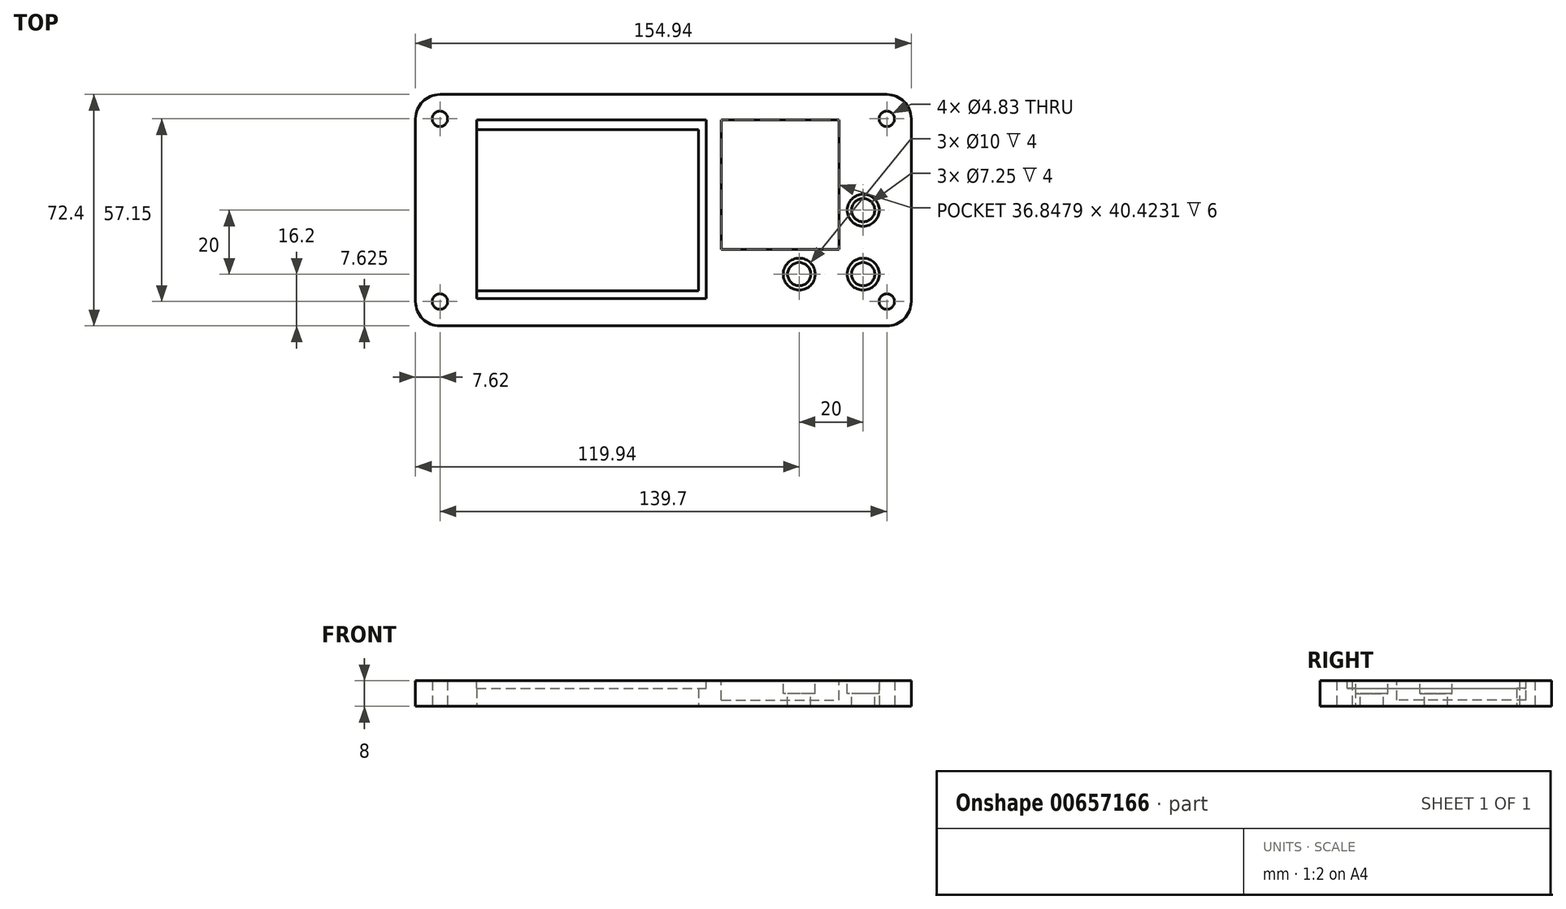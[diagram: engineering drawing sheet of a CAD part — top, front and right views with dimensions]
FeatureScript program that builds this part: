
annotation { "Feature Type Name" : "Feature", "Feature Type Description" : "" }
export const myFeature = defineFeature(function(context is Context, id is Id, definition is map)
    precondition{}
    {
        {
            var Q0;
            Q0=qCreatedBy(makeId("Top.planeOp"),FACE);
            var sketch = newSketch(context, id + "F0", { "sketchPlane" : qUnion([Q0])});
            skCircle(sketch, "E0", {"center": v(-69.85, 28.58) * mm, "radius": 2.41 * mm});
            skCircle(sketch, "E1.MirrorC", {"center": v(69.85, 28.58) * mm, "radius": 2.41 * mm});
            skCircle(sketch, "E2.MirrorC", {"center": v(-69.85, -28.58) * mm, "radius": 2.41 * mm});
            skCircle(sketch, "E3.MirrorC", {"center": v(69.85, -28.58) * mm, "radius": 2.41 * mm});
            skLineSegment(sketch, "E4", {"start": v(-77.47, 28.58) * mm, "end": v(-77.47, 0) * mm});
            skLineSegment(sketch, "E5", {"start": v(-69.85, 36.2) * mm, "end": v(0, 36.2) * mm});
            skLineSegment(sketch, "E6.MirrorCS", {"start": v(77.47, 28.58) * mm, "end": v(77.47, 0) * mm});
            skLineSegment(sketch, "E7.MirrorCS", {"start": v(69.85, 36.2) * mm, "end": v(0, 36.2) * mm});
            skLineSegment(sketch, "E8.MirrorCS", {"start": v(-77.47, -28.58) * mm, "end": v(-77.47, 0) * mm});
            skLineSegment(sketch, "E9.MirrorCS", {"start": v(-69.85, -36.2) * mm, "end": v(0, -36.2) * mm});
            skLineSegment(sketch, "E10.MirrorCS", {"start": v(69.85, -36.2) * mm, "end": v(0, -36.2) * mm});
            skLineSegment(sketch, "E11.MirrorCS", {"start": v(77.47, -28.58) * mm, "end": v(77.47, 0) * mm});
            skArc(sketch, "E12", {"start": v(-69.85, 36.2) * mm, "mid": v(-75.24, 33.96) * mm, "end": v(-77.47, 28.58) * mm});
            skArc(sketch, "E13.MirrorCS", {"start": v(69.85, 36.2) * mm, "mid": v(75.24, 33.96) * mm, "end": v(77.47, 28.58) * mm});
            skArc(sketch, "E14.MirrorCS", {"start": v(-69.85, -36.2) * mm, "mid": v(-75.24, -33.96) * mm, "end": v(-77.47, -28.58) * mm});
            skArc(sketch, "E15.MirrorCS", {"start": v(69.85, -36.2) * mm, "mid": v(75.24, -33.96) * mm, "end": v(77.47, -28.58) * mm});
            skSolve(sketch);
        }
        {
            var Q0;
            Q0=makeQuery(id+"F0.imprint","IMPRINT",FACE,{"disambiguationData":[TD([[makeQuery(id+"F0.imprint","IMPRINT",EDGE,{"derivedFrom":sQuery(id+"F0.wireOp",EDGE,"E0")}),-1.0]])]});
            extrude(context, id + "F1", {"entities" : qUnion([Q0]), "depth" : 8 * mm, "offsetDistance" : 25.4 * mm});
        }
        {
            var Q0;
            Q0=makeQuery(id+"F1.opExtrude","CAP_FACE",FACE,{"disambiguationData":[OSD([sQuery(id+"F0.wireOp",EDGE,"E0"),sQuery(id+"F0.wireOp",EDGE,"E1.MirrorC"),sQuery(id+"F0.wireOp",EDGE,"E2.MirrorC"),sQuery(id+"F0.wireOp",EDGE,"E3.MirrorC"),sQuery(id+"F0.wireOp",EDGE,"E4"),sQuery(id+"F0.wireOp",EDGE,"E5"),sQuery(id+"F0.wireOp",EDGE,"E6.MirrorCS"),sQuery(id+"F0.wireOp",EDGE,"E7.MirrorCS"),sQuery(id+"F0.wireOp",EDGE,"E8.MirrorCS"),sQuery(id+"F0.wireOp",EDGE,"E9.MirrorCS"),sQuery(id+"F0.wireOp",EDGE,"E10.MirrorCS"),sQuery(id+"F0.wireOp",EDGE,"E11.MirrorCS"),sQuery(id+"F0.wireOp",EDGE,"E12"),sQuery(id+"F0.wireOp",EDGE,"E13.MirrorCS"),sQuery(id+"F0.wireOp",EDGE,"E14.MirrorCS"),sQuery(id+"F0.wireOp",EDGE,"E15.MirrorCS")])],"isStart":true});
            var sketch = newSketch(context, id + "F2", { "sketchPlane" : qUnion([Q0])});
            skLineSegment(sketch, "E16.bottom", {"start": v(-58.42, 25.2) * mm, "end": v(10.94, 25.2) * mm});
            skLineSegment(sketch, "E16.top", {"start": v(-58.42, -25.2) * mm, "end": v(10.94, -25.2) * mm});
            skLineSegment(sketch, "E16.left", {"start": v(-58.42, 25.2) * mm, "end": v(-58.42, -25.2) * mm});
            skLineSegment(sketch, "E16.right", {"start": v(10.94, 25.2) * mm, "end": v(10.94, -25.2) * mm});
            skSolve(sketch);
        }
        {
            var Q0;
            Q0=makeQuery(id+"F2.imprint","IMPRINT",FACE,{"disambiguationData":[TD([[makeQuery(id+"F2.imprint","IMPRINT",EDGE,{"derivedFrom":sQuery(id+"F2.wireOp",EDGE,"E16.bottom")}),-1.0]])]});
            extrude(context, id + "F3", {"entities" : qUnion([Q0]), "operationType" : NewBodyOperationType.REMOVE, "oppositeDirection" : true, "depth" : 25.4 * mm, "offsetDistance" : 25.4 * mm});
        }
        {
            var Q0;
            Q0=makeQuery(id+"F1.opExtrude","CAP_FACE",FACE,{"disambiguationData":[OSD([sQuery(id+"F0.wireOp",EDGE,"E0"),sQuery(id+"F0.wireOp",EDGE,"E1.MirrorC"),sQuery(id+"F0.wireOp",EDGE,"E2.MirrorC"),sQuery(id+"F0.wireOp",EDGE,"E3.MirrorC"),sQuery(id+"F0.wireOp",EDGE,"E4"),sQuery(id+"F0.wireOp",EDGE,"E5"),sQuery(id+"F0.wireOp",EDGE,"E6.MirrorCS"),sQuery(id+"F0.wireOp",EDGE,"E7.MirrorCS"),sQuery(id+"F0.wireOp",EDGE,"E8.MirrorCS"),sQuery(id+"F0.wireOp",EDGE,"E9.MirrorCS"),sQuery(id+"F0.wireOp",EDGE,"E10.MirrorCS"),sQuery(id+"F0.wireOp",EDGE,"E11.MirrorCS"),sQuery(id+"F0.wireOp",EDGE,"E12"),sQuery(id+"F0.wireOp",EDGE,"E13.MirrorCS"),sQuery(id+"F0.wireOp",EDGE,"E14.MirrorCS"),sQuery(id+"F0.wireOp",EDGE,"E15.MirrorCS")])],"isStart":false});
            var sketch = newSketch(context, id + "F4", { "sketchPlane" : qUnion([Q0])});
            skLineSegment(sketch, "E17.bottom", {"start": v(-58.42, -27.7) * mm, "end": v(13.44, -27.7) * mm});
            skLineSegment(sketch, "E17.top", {"start": v(-58.42, 28.2) * mm, "end": v(13.44, 28.2) * mm});
            skLineSegment(sketch, "E17.left", {"start": v(-58.42, -27.7) * mm, "end": v(-58.42, 28.2) * mm});
            skLineSegment(sketch, "E17.right", {"start": v(13.44, -27.7) * mm, "end": v(13.44, 28.2) * mm});
            skSolve(sketch);
        }
        {
            var Q0;
            {var subQ1=makeQuery(id+"F1.opExtrude","CAP_FACE",FACE,{"disambiguationData":[OSD([sQuery(id+"F0.wireOp",EDGE,"E0"),sQuery(id+"F0.wireOp",EDGE,"E1.MirrorC"),sQuery(id+"F0.wireOp",EDGE,"E2.MirrorC"),sQuery(id+"F0.wireOp",EDGE,"E3.MirrorC"),sQuery(id+"F0.wireOp",EDGE,"E4"),sQuery(id+"F0.wireOp",EDGE,"E5"),sQuery(id+"F0.wireOp",EDGE,"E6.MirrorCS"),sQuery(id+"F0.wireOp",EDGE,"E7.MirrorCS"),sQuery(id+"F0.wireOp",EDGE,"E8.MirrorCS"),sQuery(id+"F0.wireOp",EDGE,"E9.MirrorCS"),sQuery(id+"F0.wireOp",EDGE,"E10.MirrorCS"),sQuery(id+"F0.wireOp",EDGE,"E11.MirrorCS"),sQuery(id+"F0.wireOp",EDGE,"E12"),sQuery(id+"F0.wireOp",EDGE,"E13.MirrorCS"),sQuery(id+"F0.wireOp",EDGE,"E14.MirrorCS"),sQuery(id+"F0.wireOp",EDGE,"E15.MirrorCS")])],"isStart":false});var subQ2=makeQuery(id+"F3.boolean.opBoolean","INTERSECT",EDGE,{"derivedFrom":[subQ1,makeQuery(id+"F3.opExtrude","SWEPT_FACE",FACE,{"disambiguationData":[OSD([sQuery(id+"F2.wireOp",EDGE,"E16.bottom")])]})]});Q0=makeQuery(id+"F4.imprint","IMPRINT",FACE,{"disambiguationData":[TD([[makeQuery(id+"F4.imprint","IMPRINT",EDGE,{"derivedFrom":subQ2}),-1.0]])]});}
            var Q1;
            {var subQ5=sQuery(id+"F4.wireOp",EDGE,"E17.bottom");Q1=makeQuery(id+"F4.imprint","IMPRINT",FACE,{"disambiguationData":[TD([[makeQuery(id+"F4.imprint","IMPRINT",EDGE,{"derivedFrom":subQ5}),1.0]])]});}
            extrude(context, id + "F5", {"entities" : qUnion([Q0, Q1]), "operationType" : NewBodyOperationType.REMOVE, "oppositeDirection" : true, "depth" : 2.35 * mm, "offsetDistance" : 25.4 * mm});
        }
        {
            var Q0;
            Q0=makeQuery(id+"F1.opExtrude","CAP_FACE",FACE,{"disambiguationData":[OSD([sQuery(id+"F0.wireOp",EDGE,"E0"),sQuery(id+"F0.wireOp",EDGE,"E1.MirrorC"),sQuery(id+"F0.wireOp",EDGE,"E2.MirrorC"),sQuery(id+"F0.wireOp",EDGE,"E3.MirrorC"),sQuery(id+"F0.wireOp",EDGE,"E4"),sQuery(id+"F0.wireOp",EDGE,"E5"),sQuery(id+"F0.wireOp",EDGE,"E6.MirrorCS"),sQuery(id+"F0.wireOp",EDGE,"E7.MirrorCS"),sQuery(id+"F0.wireOp",EDGE,"E8.MirrorCS"),sQuery(id+"F0.wireOp",EDGE,"E9.MirrorCS"),sQuery(id+"F0.wireOp",EDGE,"E10.MirrorCS"),sQuery(id+"F0.wireOp",EDGE,"E11.MirrorCS"),sQuery(id+"F0.wireOp",EDGE,"E12"),sQuery(id+"F0.wireOp",EDGE,"E13.MirrorCS"),sQuery(id+"F0.wireOp",EDGE,"E14.MirrorCS"),sQuery(id+"F0.wireOp",EDGE,"E15.MirrorCS")])],"isStart":false});
            extrude(context, id + "F6", {"entities" : qUnion([Q0]), "operationType" : NewBodyOperationType.ADD, "depth" : 2 * mm, "offsetDistance" : 25.4 * mm});
        }
        {
            var Q0;
            Q0=makeQuery(id+"F6.opExtrude","CAP_FACE",FACE,{"disambiguationData":[OSD([sQuery(id+"F0.wireOp",EDGE,"E0"),sQuery(id+"F0.wireOp",EDGE,"E1.MirrorC"),sQuery(id+"F0.wireOp",EDGE,"E2.MirrorC"),sQuery(id+"F0.wireOp",EDGE,"E3.MirrorC"),sQuery(id+"F0.wireOp",EDGE,"E4"),sQuery(id+"F0.wireOp",EDGE,"E5"),sQuery(id+"F0.wireOp",EDGE,"E6.MirrorCS"),sQuery(id+"F0.wireOp",EDGE,"E7.MirrorCS"),sQuery(id+"F0.wireOp",EDGE,"E8.MirrorCS"),sQuery(id+"F0.wireOp",EDGE,"E9.MirrorCS"),sQuery(id+"F0.wireOp",EDGE,"E10.MirrorCS"),sQuery(id+"F0.wireOp",EDGE,"E11.MirrorCS"),sQuery(id+"F0.wireOp",EDGE,"E12"),sQuery(id+"F0.wireOp",EDGE,"E13.MirrorCS"),sQuery(id+"F0.wireOp",EDGE,"E14.MirrorCS"),sQuery(id+"F0.wireOp",EDGE,"E15.MirrorCS")])],"isStart":false});
            var sketch = newSketch(context, id + "F7", { "sketchPlane" : qUnion([Q0])});
            skCircle(sketch, "E18", {"center": v(62.47, -20) * mm, "radius": 5 * mm});
            skCircle(sketch, "E19", {"center": v(42.47, -20) * mm, "radius": 5 * mm});
            skCircle(sketch, "E20", {"center": v(62.47, 0) * mm, "radius": 5 * mm});
            skSolve(sketch);
        }
        {
            var Q0;
            Q0 = qSketchRegion(id + "F7", true);
            extrude(context, id + "F8", {"entities" : qUnion([Q0]), "operationType" : NewBodyOperationType.REMOVE, "oppositeDirection" : true, "depth" : 6 * mm, "offsetDistance" : 25.4 * mm});
        }
        {
            var Q0;
            Q0=makeQuery(id+"F8.boolean.opBoolean","COPY",FACE,{"derivedFrom":makeQuery(id+"F8.opExtrude","CAP_FACE",FACE,{"disambiguationData":[OSD([sQuery(id+"F7.wireOp",EDGE,"E20")])],"isStart":false})});
            var sketch = newSketch(context, id + "F9", { "sketchPlane" : qUnion([Q0])});
            skCircle(sketch, "E21", {"center": v(62.47, 0) * mm, "radius": 3.62 * mm});
            skSolve(sketch);
        }
        {
            var Q0;
            Q0 = qSketchRegion(id + "F9", true);
            extrude(context, id + "F10", {"entities" : qUnion([Q0]), "operationType" : NewBodyOperationType.REMOVE, "oppositeDirection" : true, "depth" : 25.4 * mm, "offsetDistance" : 25.4 * mm});
        }
        {
            var Q0;
            Q0=makeQuery(id+"F8.boolean.opBoolean","COPY",FACE,{"derivedFrom":makeQuery(id+"F8.opExtrude","CAP_FACE",FACE,{"disambiguationData":[OSD([sQuery(id+"F7.wireOp",EDGE,"E18")])],"isStart":false})});
            var sketch = newSketch(context, id + "F11", { "sketchPlane" : qUnion([Q0])});
            skCircle(sketch, "E22", {"center": v(62.47, -20) * mm, "radius": 3.63 * mm});
            skSolve(sketch);
        }
        {
            var Q0;
            Q0 = qSketchRegion(id + "F11", true);
            extrude(context, id + "F12", {"entities" : qUnion([Q0]), "operationType" : NewBodyOperationType.REMOVE, "oppositeDirection" : true, "depth" : 25.4 * mm, "offsetDistance" : 25.4 * mm});
        }
        {
            var Q0;
            Q0=makeQuery(id+"F8.boolean.opBoolean","COPY",FACE,{"derivedFrom":makeQuery(id+"F8.opExtrude","CAP_FACE",FACE,{"disambiguationData":[OSD([sQuery(id+"F7.wireOp",EDGE,"E19")])],"isStart":false})});
            var sketch = newSketch(context, id + "F13", { "sketchPlane" : qUnion([Q0])});
            skCircle(sketch, "E23", {"center": v(42.47, -20) * mm, "radius": 3.62 * mm});
            skSolve(sketch);
        }
        {
            var Q0;
            Q0 = qSketchRegion(id + "F13", true);
            extrude(context, id + "F14", {"entities" : qUnion([Q0]), "operationType" : NewBodyOperationType.REMOVE, "oppositeDirection" : true, "depth" : 25.4 * mm, "offsetDistance" : 25.4 * mm});
        }
        {
            var Q0;
            Q0=makeQuery(id+"F6.opExtrude","CAP_FACE",FACE,{"disambiguationData":[OSD([sQuery(id+"F0.wireOp",EDGE,"E0"),sQuery(id+"F0.wireOp",EDGE,"E1.MirrorC"),sQuery(id+"F0.wireOp",EDGE,"E2.MirrorC"),sQuery(id+"F0.wireOp",EDGE,"E3.MirrorC"),sQuery(id+"F0.wireOp",EDGE,"E4"),sQuery(id+"F0.wireOp",EDGE,"E5"),sQuery(id+"F0.wireOp",EDGE,"E6.MirrorCS"),sQuery(id+"F0.wireOp",EDGE,"E7.MirrorCS"),sQuery(id+"F0.wireOp",EDGE,"E8.MirrorCS"),sQuery(id+"F0.wireOp",EDGE,"E9.MirrorCS"),sQuery(id+"F0.wireOp",EDGE,"E10.MirrorCS"),sQuery(id+"F0.wireOp",EDGE,"E11.MirrorCS"),sQuery(id+"F0.wireOp",EDGE,"E12"),sQuery(id+"F0.wireOp",EDGE,"E13.MirrorCS"),sQuery(id+"F0.wireOp",EDGE,"E14.MirrorCS"),sQuery(id+"F0.wireOp",EDGE,"E15.MirrorCS")])],"isStart":false});
            var sketch = newSketch(context, id + "F15", { "sketchPlane" : qUnion([Q0])});
            skSolve(sketch);
        }
        {
            var Q0;
            {var subQ10=sQuery(id+"F0.wireOp",EDGE,"E0");Q0=makeQuery(id+"F15.imprint","IMPRINT",FACE,{"disambiguationData":[TD([[makeQuery(id+"F15.imprint","IMPRINT",EDGE,{"derivedFrom":makeQuery(id+"F6.opExtrude","CAP_EDGE",EDGE,{"disambiguationData":[OSD([subQ10])],"isStart":false})}),-1.0]])]});}
            extrude(context, id + "F16", {"entities" : qUnion([Q0]), "operationType" : NewBodyOperationType.REMOVE, "oppositeDirection" : true, "depth" : 2 * mm, "offsetDistance" : 25.4 * mm});
        }
        {
            var Q0;
            Q0=makeQuery(id+"F16.boolean.opBoolean","COPY",FACE,{"derivedFrom":makeQuery(id+"F16.opExtrude","CAP_FACE",FACE,{"disambiguationData":[OSD([sQuery(id+"F0.wireOp",EDGE,"E0"),sQuery(id+"F0.wireOp",EDGE,"E1.MirrorC"),sQuery(id+"F0.wireOp",EDGE,"E2.MirrorC"),sQuery(id+"F0.wireOp",EDGE,"E3.MirrorC"),sQuery(id+"F0.wireOp",EDGE,"E4"),sQuery(id+"F0.wireOp",EDGE,"E5"),sQuery(id+"F0.wireOp",EDGE,"E6.MirrorCS"),sQuery(id+"F0.wireOp",EDGE,"E7.MirrorCS"),sQuery(id+"F0.wireOp",EDGE,"E8.MirrorCS"),sQuery(id+"F0.wireOp",EDGE,"E9.MirrorCS"),sQuery(id+"F0.wireOp",EDGE,"E10.MirrorCS"),sQuery(id+"F0.wireOp",EDGE,"E11.MirrorCS"),sQuery(id+"F0.wireOp",EDGE,"E12"),sQuery(id+"F0.wireOp",EDGE,"E13.MirrorCS"),sQuery(id+"F0.wireOp",EDGE,"E14.MirrorCS"),sQuery(id+"F0.wireOp",EDGE,"E15.MirrorCS"),sQuery(id+"F2.wireOp",EDGE,"E16.left"),sQuery(id+"F4.wireOp",EDGE,"E17.bottom"),sQuery(id+"F4.wireOp",EDGE,"E17.top"),sQuery(id+"F4.wireOp",EDGE,"E17.left"),sQuery(id+"F4.wireOp",EDGE,"E17.right"),sQuery(id+"F7.wireOp",EDGE,"E18"),sQuery(id+"F7.wireOp",EDGE,"E19"),sQuery(id+"F7.wireOp",EDGE,"E20")])],"isStart":false})});
            var sketch = newSketch(context, id + "F17", { "sketchPlane" : qUnion([Q0])});
            skLineSegment(sketch, "E24.bottom", {"start": v(18.1, 28.2) * mm, "end": v(54.95, 28.2) * mm});
            skLineSegment(sketch, "E24.top", {"start": v(18.1, -12.23) * mm, "end": v(54.95, -12.23) * mm});
            skLineSegment(sketch, "E24.left", {"start": v(18.1, 28.2) * mm, "end": v(18.1, -12.23) * mm});
            skLineSegment(sketch, "E24.right", {"start": v(54.95, 28.2) * mm, "end": v(54.95, -12.23) * mm});
            skSolve(sketch);
        }
        {
            var Q0;
            Q0=makeQuery(id+"F17.imprint","IMPRINT",FACE,{"disambiguationData":[TD([[makeQuery(id+"F17.imprint","IMPRINT",EDGE,{"derivedFrom":sQuery(id+"F17.wireOp",EDGE,"E24.bottom")}),-1.0]])]});
            extrude(context, id + "F18", {"entities" : qUnion([Q0]), "operationType" : NewBodyOperationType.REMOVE, "oppositeDirection" : true, "depth" : 6 * mm, "offsetDistance" : 25 * mm});
        }
    });
